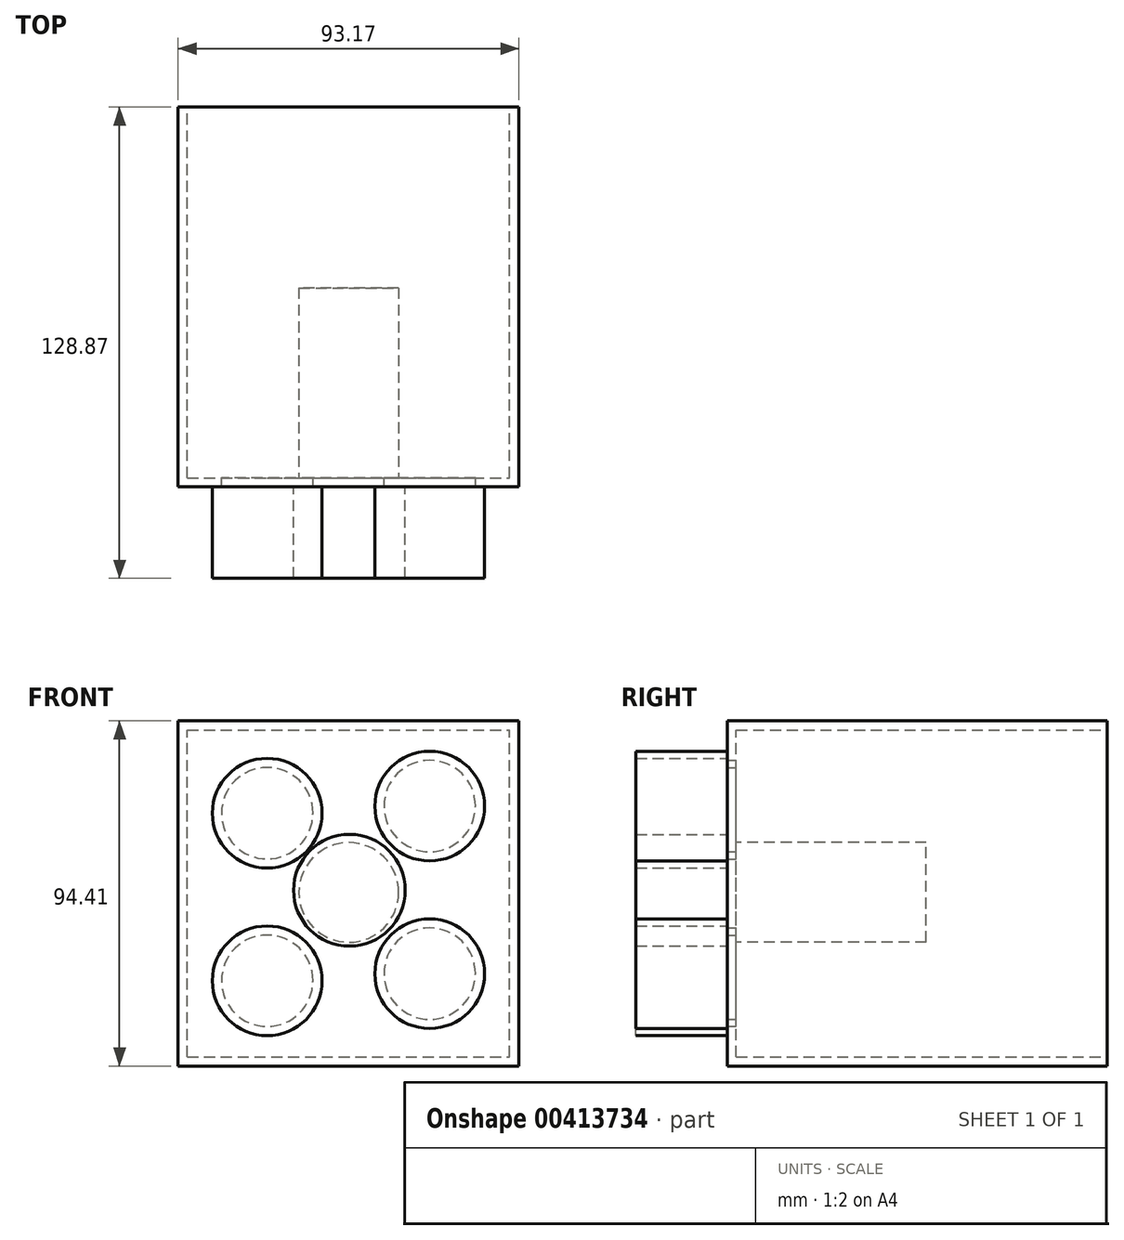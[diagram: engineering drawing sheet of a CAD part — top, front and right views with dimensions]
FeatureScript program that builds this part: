
annotation { "Feature Type Name" : "Feature", "Feature Type Description" : "" }
export const myFeature = defineFeature(function(context is Context, id is Id, definition is map)
    precondition{}
    {
        {
            var Q0;
            Q0=qCreatedBy(makeId("Front.planeOp"),FACE);
            cPlane(context, id + "F0", {"entities" : qUnion([Q0]), "cplaneType" : CPlaneType.OFFSET, "offset" : 12.57 * mm, "oppositeDirection" : true, "width" : 150 * mm, "height" : 150 * mm});
        }
        {
            var Q0;
            Q0=qCreatedBy(id+"F0.planeOp",FACE);
            var sketch = newSketch(context, id + "F1", { "sketchPlane" : qUnion([Q0])});
            skLineSegment(sketch, "E0.bottom", {"start": v(-32.6, -38.19) * mm, "end": v(60.56, -38.19) * mm});
            skLineSegment(sketch, "E0.top", {"start": v(-32.6, 56.22) * mm, "end": v(60.56, 56.22) * mm});
            skLineSegment(sketch, "E0.left", {"start": v(-32.6, -38.19) * mm, "end": v(-32.6, 56.22) * mm});
            skLineSegment(sketch, "E0.right", {"start": v(60.56, -38.19) * mm, "end": v(60.56, 56.22) * mm});
            skSolve(sketch);
        }
        {
            var Q0;
            Q0 = qSketchRegion(id + "F1", true);
            extrude(context, id + "F2", {"entities" : qUnion([Q0]), "depth" : 103.86 * mm});
        }
        {
            var Q0;
            Q0=makeQuery(id+"F2.opExtrude","CAP_FACE",FACE,{"disambiguationData":[OSD([sQuery(id+"F1.wireOp",EDGE,"E0.bottom"),sQuery(id+"F1.wireOp",EDGE,"E0.top"),sQuery(id+"F1.wireOp",EDGE,"E0.left"),sQuery(id+"F1.wireOp",EDGE,"E0.right")])],"isStart":false});
            var sketch = newSketch(context, id + "F3", { "sketchPlane" : qUnion([Q0])});
            skCircle(sketch, "E1", {"center": v(36.2, 32.91) * mm, "radius": 15 * mm});
            skCircle(sketch, "E2", {"center": v(36.2, -12.93) * mm, "radius": 15 * mm});
            skCircle(sketch, "E3", {"center": v(-8.24, -14.88) * mm, "radius": 15 * mm});
            skCircle(sketch, "E4", {"center": v(-8.24, 30.96) * mm, "radius": 15 * mm});
            skLineSegment(sketch, "E5", {"start": v(36.2, -12.93) * mm, "end": v(-8.24, -14.88) * mm, "construction": true});
            skLineSegment(sketch, "E6", {"start": v(36.2, 32.91) * mm, "end": v(-8.24, 30.96) * mm, "construction": true});
            skLineSegment(sketch, "E7", {"start": v(36.2, 32.91) * mm, "end": v(36.2, -12.93) * mm, "construction": true});
            skLineSegment(sketch, "E8", {"start": v(-8.24, -14.88) * mm, "end": v(-8.24, 30.96) * mm, "construction": true});
            skLineSegment(sketch, "E9", {"start": v(-32.6, 56.22) * mm, "end": v(60.56, -38.19) * mm, "construction": true});
            skPoint(sketch, "E10", {"position": v(13.98, 9.02) * mm});
            skLineSegment(sketch, "E11", {"start": v(36.2, 32.91) * mm, "end": v(-8.24, -14.88) * mm, "construction": true});
            skSolve(sketch);
        }
        {
            var Q0;
            Q0 = qSketchRegion(id + "F3", true);
            extrude(context, id + "F4", {"entities" : qUnion([Q0]), "operationType" : NewBodyOperationType.ADD, "depth" : 25 * mm});
        }
        {
            var Q0;
            Q0=makeQuery(id+"F2.opExtrude","CAP_FACE",FACE,{"disambiguationData":[OSD([sQuery(id+"F1.wireOp",EDGE,"E0.bottom"),sQuery(id+"F1.wireOp",EDGE,"E0.top"),sQuery(id+"F1.wireOp",EDGE,"E0.left"),sQuery(id+"F1.wireOp",EDGE,"E0.right")])],"isStart":true});
            shell(context, id + "F5", {"entities" : qUnion([Q0]), "thickness" : 2.5 * mm});
        }
        {
            var Q0;
            Q0 = qSketchRegion(id + "F3", true);
            extrude(context, id + "F6", {"entities" : qUnion([Q0]), "operationType" : NewBodyOperationType.ADD, "depth" : 25 * mm});
        }
        {
            var Q0;
            Q0 = qSketchRegion(id + "F3", true);
            var sketch = newSketch(context, id + "F7", { "sketchPlane" : qUnion([Q0])});
            skCircle(sketch, "E12", {"center": v(14.25, 9.89) * mm, "radius": 15.27 * mm});
            skSolve(sketch);
        }
        {
            var Q0;
            Q0 = qSketchRegion(id + "F7", true);
            extrude(context, id + "F8", {"entities" : qUnion([Q0]), "operationType" : NewBodyOperationType.ADD, "depth" : 25 * mm});
        }
        {
            var Q0;
            Q0 = qSketchRegion(id + "F3", true);
            var sketch = newSketch(context, id + "F9", { "sketchPlane" : qUnion([Q0])});
            skCircle(sketch, "E13", {"center": v(14.05, 9.29) * mm, "radius": 13.63 * mm});
            skSolve(sketch);
        }
        {
            var Q0;
            Q0 = qSketchRegion(id + "F9", true);
            extrude(context, id + "F10", {"entities" : qUnion([Q0]), "operationType" : NewBodyOperationType.ADD, "oppositeDirection" : true, "depth" : 54.43 * mm});
        }
    });
